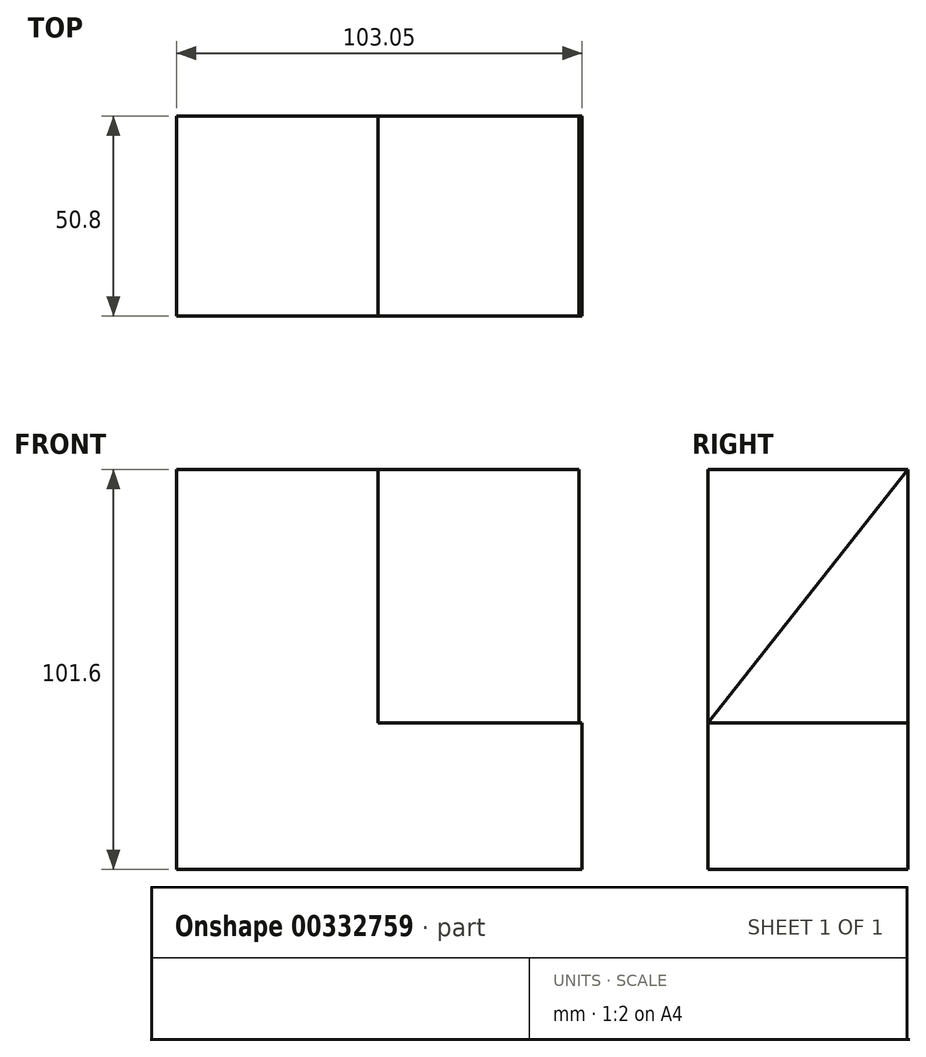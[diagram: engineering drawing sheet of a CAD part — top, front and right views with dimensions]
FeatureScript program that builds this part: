
annotation { "Feature Type Name" : "Feature", "Feature Type Description" : "" }
export const myFeature = defineFeature(function(context is Context, id is Id, definition is map)
    precondition{}
    {
        {
            var Q0;
            Q0=qCreatedBy(makeId("Front.planeOp"),FACE);
            var sketch = newSketch(context, id + "F0", { "sketchPlane" : qUnion([Q0])});
            skLineSegment(sketch, "E0", {"start": v(-57.4, 53.7) * mm, "end": v(-57.4, -47.9) * mm});
            skLineSegment(sketch, "E1", {"start": v(-57.4, -47.9) * mm, "end": v(45.64, -47.9) * mm});
            skLineSegment(sketch, "E2", {"start": v(45.64, -47.9) * mm, "end": v(45.64, -24.19) * mm});
            skLineSegment(sketch, "E3", {"start": v(44.68, -10.64) * mm, "end": v(-6.12, -10.64) * mm});
            skLineSegment(sketch, "E4", {"start": v(-6.12, -10.64) * mm, "end": v(-6.12, 53.7) * mm});
            skLineSegment(sketch, "E5", {"start": v(-6.12, 53.7) * mm, "end": v(-57.4, 53.7) * mm});
            skLineSegment(sketch, "E6", {"start": v(45.64, -24.19) * mm, "end": v(45.64, -10.64) * mm});
            skLineSegment(sketch, "E7", {"start": v(45.64, -10.64) * mm, "end": v(44.68, -10.64) * mm});
            skSolve(sketch);
        }
        {
            var Q0;
            Q0=makeQuery(id+"F0.imprint","IMPRINT",FACE,{"disambiguationData":[TD([[makeQuery(id+"F0.imprint","IMPRINT",EDGE,{"derivedFrom":sQuery(id+"F0.wireOp",EDGE,"E0")}),1.0]])]});
            extrude(context, id + "F1", {"entities" : qUnion([Q0]), "depth" : 50.8 * mm});
        }
        {
            var Q0;
            Q0=makeQuery(id+"F1.opExtrude","SWEPT_FACE",FACE,{"disambiguationData":[OSD([sQuery(id+"F0.wireOp",EDGE,"E4")])]});
            var sketch = newSketch(context, id + "F2", { "sketchPlane" : qUnion([Q0])});
            skLineSegment(sketch, "E8", {"start": v(-50.8, -10.64) * mm, "end": v(0, 53.7) * mm});
            skLineSegment(sketch, "E9", {"start": v(-50.8, -10.64) * mm, "end": v(0, -10.64) * mm});
            skLineSegment(sketch, "E10", {"start": v(0, -10.64) * mm, "end": v(0, 53.7) * mm});
            skSolve(sketch);
        }
        {
            var Q0;
            Q0=makeQuery(id+"F2.imprint","IMPRINT",FACE,{"disambiguationData":[TD([[makeQuery(id+"F2.imprint","IMPRINT",EDGE,{"derivedFrom":sQuery(id+"F2.wireOp",EDGE,"E8")}),-1.0]])]});
            extrude(context, id + "F3", {"entities" : qUnion([Q0]), "operationType" : NewBodyOperationType.ADD, "depth" : 51.05 * mm});
        }
    });
